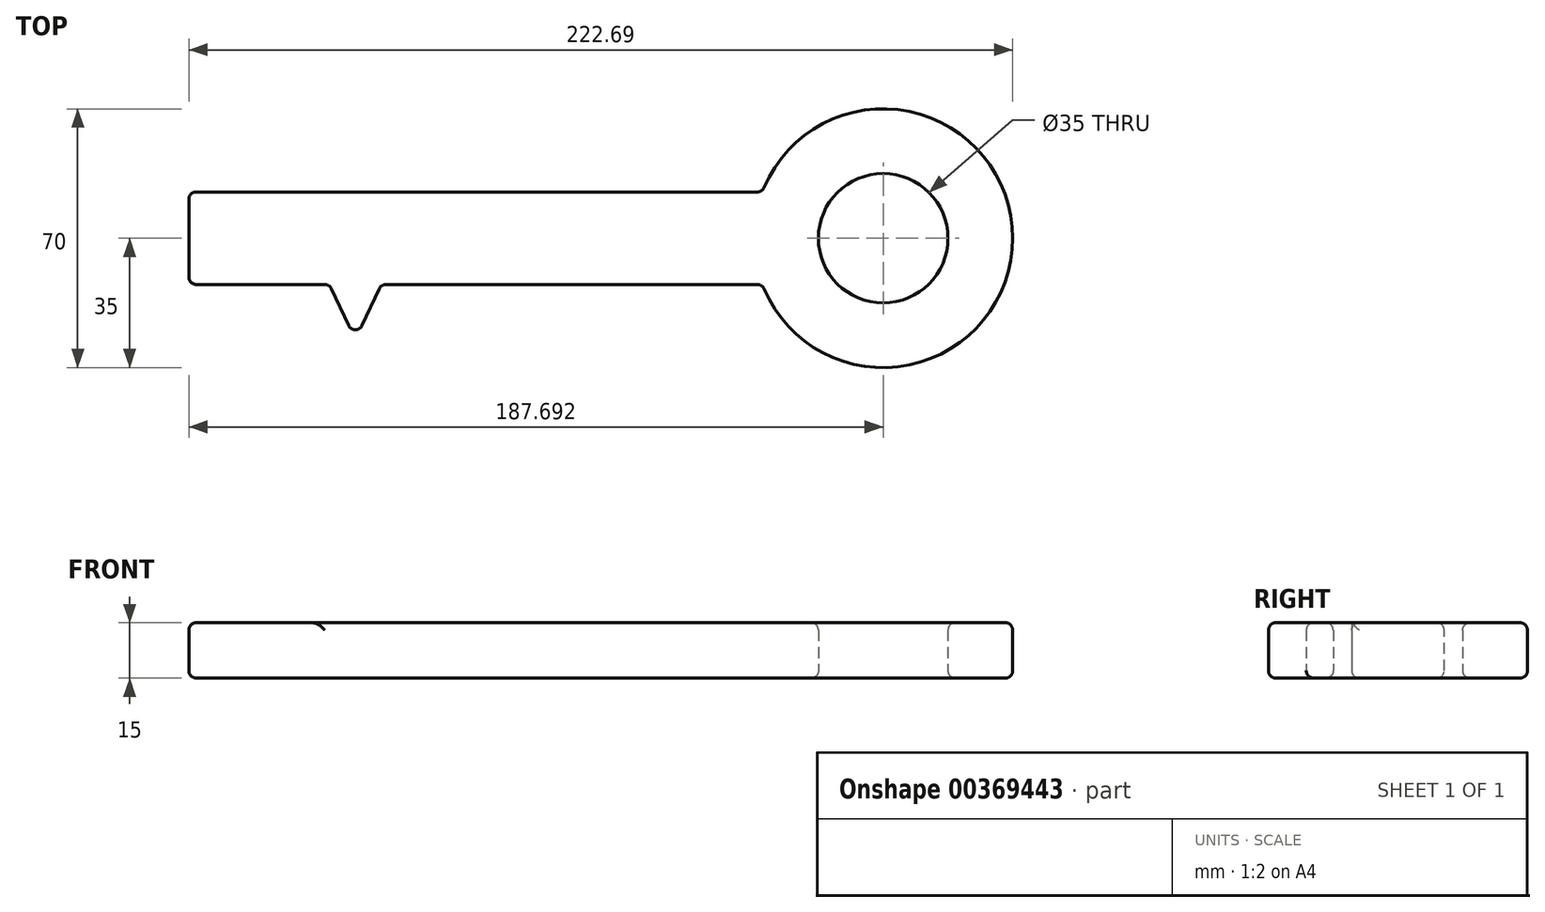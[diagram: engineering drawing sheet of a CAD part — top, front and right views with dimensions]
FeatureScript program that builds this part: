
annotation { "Feature Type Name" : "Feature", "Feature Type Description" : "" }
export const myFeature = defineFeature(function(context is Context, id is Id, definition is map)
    precondition{}
    {
        {
            var Q0;
            Q0=qCreatedBy(makeId("Top.planeOp"),FACE);
            var sketch = newSketch(context, id + "F0", { "sketchPlane" : qUnion([Q0])});
            skLineSegment(sketch, "E0.bottom", {"start": v(0, 10.7) * mm, "end": v(-155, 10.7) * mm});
            skLineSegment(sketch, "E0.top", {"start": v(0, 35.7) * mm, "end": v(-155, 35.7) * mm});
            skLineSegment(sketch, "E0.left", {"start": v(0, 10.7) * mm, "end": v(0, 35.7) * mm});
            skLineSegment(sketch, "E0.right", {"start": v(-155, 10.7) * mm, "end": v(-155, 35.7) * mm});
            skLineSegment(sketch, "E1.bottom", {"start": v(-155, 10.7) * mm, "end": v(-145, 10.7) * mm});
            skLineSegment(sketch, "E1.top", {"start": v(-155, -19.3) * mm, "end": v(-145, -19.3) * mm});
            skLineSegment(sketch, "E1.left", {"start": v(-155, 10.7) * mm, "end": v(-155, -19.3) * mm});
            skLineSegment(sketch, "E1.right", {"start": v(-145, 10.7) * mm, "end": v(-145, -19.3) * mm});
            skLineSegment(sketch, "E2.bottom", {"start": v(-135, 10.7) * mm, "end": v(-127, 10.7) * mm});
            skLineSegment(sketch, "E2.top", {"start": v(-135, -4.3) * mm, "end": v(-127, -4.3) * mm});
            skLineSegment(sketch, "E2.left", {"start": v(-135, 10.7) * mm, "end": v(-135, -4.3) * mm});
            skLineSegment(sketch, "E2.right", {"start": v(-127, 10.7) * mm, "end": v(-127, -4.3) * mm});
            skLineSegment(sketch, "E3", {"start": v(-103, 10.7) * mm, "end": v(-110, -4.3) * mm});
            skLineSegment(sketch, "E4", {"start": v(-110, -4.3) * mm, "end": v(-117, 10.7) * mm});
            skLineSegment(sketch, "E5", {"start": v(-117, 10.7) * mm, "end": v(-103, 10.7) * mm});
            skArc(sketch, "E6", {"start": v(0, 10.7) * mm, "mid": v(67.7, 23.2) * mm, "end": v(0, 35.7) * mm});
            skCircle(sketch, "E7", {"center": v(32.7, 23.2) * mm, "radius": 17.5 * mm});
            skLineSegment(sketch, "E8", {"start": v(32.7, 23.2) * mm, "end": v(-155, 23.2) * mm, "construction": true});
            skSolve(sketch);
        }
        {
            var Q0;
            Q0=makeQuery(id+"F0.imprint","IMPRINT",FACE,{"disambiguationData":[TD([[makeQuery(id+"F0.imprint","IMPRINT",EDGE,{"derivedFrom":sQuery(id+"F0.wireOp",EDGE,"E1.bottom")}),-1.0]])]});
            var Q1;
            Q1=makeQuery(id+"F0.imprint","IMPRINT",FACE,{"disambiguationData":[TD([[makeQuery(id+"F0.imprint","IMPRINT",EDGE,{"derivedFrom":sQuery(id+"F0.wireOp",EDGE,"E2.bottom")}),-1.0]])]});
            var Q2;
            Q2=makeQuery(id+"F0.imprint","IMPRINT",FACE,{"disambiguationData":[TD([[makeQuery(id+"F0.imprint","IMPRINT",EDGE,{"derivedFrom":sQuery(id+"F0.wireOp",EDGE,"E3")}),-1.0]])]});
            var Q3;
            Q3=makeQuery(id+"F0.imprint","IMPRINT",FACE,{"disambiguationData":[TD([[makeQuery(id+"F0.imprint","IMPRINT",EDGE,{"derivedFrom":sQuery(id+"F0.wireOp",EDGE,"E0.left")}),-1.0]])]});
            var Q4;
            Q4=makeQuery(id+"F0.imprint","IMPRINT",FACE,{"disambiguationData":[TD([[makeQuery(id+"F0.imprint","IMPRINT",EDGE,{"derivedFrom":sQuery(id+"F0.wireOp",EDGE,"E0.top")}),1.0]])]});
            extrude(context, id + "F1", {"entities" : qUnion([Q0, Q1, Q2, Q3, Q4]), "depth" : 15 * mm});
        }
        {
            var Q0;
            Q0=makeQuery(id+"F1.opExtrude","CAP_EDGE",EDGE,{"disambiguationData":[OSD([sQuery(id+"F0.wireOp",EDGE,"E0.top")])],"isStart":false});
            var Q1;
            Q1=makeQuery(id+"F1.opExtrude","CAP_EDGE",EDGE,{"disambiguationData":[OSD([sQuery(id+"F0.wireOp",EDGE,"E6")])],"isStart":false});
            var Q2;
            Q2=makeQuery(id+"F1.opExtrude","CAP_EDGE",EDGE,{"disambiguationData":[OSD([sQuery(id+"F0.wireOp",EDGE,"E7")])],"isStart":false});
            var Q3;
            {var subQ0=sQuery(id+"F0.wireOp",EDGE,"E0.bottom");Q3=makeQuery(id+"F1.opExtrude","CAP_EDGE",EDGE,{"disambiguationData":[OSD([subQ0]),TDD([makeQuery(id+"F0.imprint","IMPRINT",EDGE,{"disambiguationData":[TD([[makeQuery(id+"F0.imprint","INTERSECT",VERTEX,{"derivedFrom":[subQ0,sQuery(id+"F0.wireOp",EDGE,"E0.left"),sQuery(id+"F0.wireOp",EDGE,"E6")]}),-1.0]])],"derivedFrom":subQ0})])],"isStart":false});}
            var Q4;
            Q4=makeQuery(id+"F1.opExtrude","CAP_EDGE",EDGE,{"disambiguationData":[OSD([sQuery(id+"F0.wireOp",EDGE,"E3")])],"isStart":false});
            var Q5;
            Q5=makeQuery(id+"F1.opExtrude","CAP_EDGE",EDGE,{"disambiguationData":[OSD([sQuery(id+"F0.wireOp",EDGE,"E4")])],"isStart":false});
            var Q6;
            Q6=makeQuery(id+"F1.opExtrude","CAP_EDGE",EDGE,{"disambiguationData":[OSD([sQuery(id+"F0.wireOp",EDGE,"E2.right")])],"isStart":false});
            var Q7;
            Q7=makeQuery(id+"F1.opExtrude","CAP_EDGE",EDGE,{"disambiguationData":[OSD([sQuery(id+"F0.wireOp",EDGE,"E2.top")])],"isStart":false});
            var Q8;
            Q8=makeQuery(id+"F1.opExtrude","CAP_EDGE",EDGE,{"disambiguationData":[OSD([sQuery(id+"F0.wireOp",EDGE,"E2.left")])],"isStart":false});
            var Q9;
            Q9=makeQuery(id+"F1.opExtrude","CAP_EDGE",EDGE,{"disambiguationData":[OSD([sQuery(id+"F0.wireOp",EDGE,"E1.right")])],"isStart":false});
            var Q10;
            Q10=makeQuery(id+"F1.opExtrude","CAP_EDGE",EDGE,{"disambiguationData":[OSD([sQuery(id+"F0.wireOp",EDGE,"E1.top")])],"isStart":false});
            var Q11;
            Q11=makeQuery(id+"F1.opExtrude","CAP_EDGE",EDGE,{"disambiguationData":[OSD([sQuery(id+"F0.wireOp",EDGE,"E0.right"),sQuery(id+"F0.wireOp",EDGE,"E1.left")])],"isStart":false});
            var Q12;
            Q12=makeQuery(id+"F1.opExtrude","CAP_EDGE",EDGE,{"disambiguationData":[OSD([sQuery(id+"F0.wireOp",EDGE,"E0.top")])],"isStart":true});
            var Q13;
            Q13=makeQuery(id+"F1.opExtrude","CAP_EDGE",EDGE,{"disambiguationData":[OSD([sQuery(id+"F0.wireOp",EDGE,"E6")])],"isStart":true});
            var Q14;
            Q14=makeQuery(id+"F1.opExtrude","CAP_EDGE",EDGE,{"disambiguationData":[OSD([sQuery(id+"F0.wireOp",EDGE,"E7")])],"isStart":true});
            var Q15;
            Q15=makeQuery(id+"F1.opExtrude","SWEPT_EDGE",EDGE,{"disambiguationData":[OSD([sQuery(id+"F0.wireOp",EDGE,"E0.bottom"),sQuery(id+"F0.wireOp",EDGE,"E3"),sQuery(id+"F0.wireOp",EDGE,"E5")])]});
            var Q16;
            Q16=makeQuery(id+"F1.opExtrude","SWEPT_EDGE",EDGE,{"disambiguationData":[OSD([sQuery(id+"F0.wireOp",EDGE,"E3"),sQuery(id+"F0.wireOp",EDGE,"E4")])]});
            var Q17;
            Q17=makeQuery(id+"F1.opExtrude","SWEPT_EDGE",EDGE,{"disambiguationData":[OSD([sQuery(id+"F0.wireOp",EDGE,"E0.bottom"),sQuery(id+"F0.wireOp",EDGE,"E4"),sQuery(id+"F0.wireOp",EDGE,"E5")])]});
            var Q18;
            Q18=makeQuery(id+"F1.opExtrude","SWEPT_EDGE",EDGE,{"disambiguationData":[OSD([sQuery(id+"F0.wireOp",EDGE,"E2.top"),sQuery(id+"F0.wireOp",EDGE,"E2.right")])]});
            var Q19;
            Q19=makeQuery(id+"F1.opExtrude","SWEPT_EDGE",EDGE,{"disambiguationData":[OSD([sQuery(id+"F0.wireOp",EDGE,"E1.top"),sQuery(id+"F0.wireOp",EDGE,"E1.right")])]});
            var Q20;
            Q20=makeQuery(id+"F1.opExtrude","SWEPT_EDGE",EDGE,{"disambiguationData":[OSD([sQuery(id+"F0.wireOp",EDGE,"E2.top"),sQuery(id+"F0.wireOp",EDGE,"E2.left")])]});
            var Q21;
            Q21=makeQuery(id+"F1.opExtrude","SWEPT_EDGE",EDGE,{"disambiguationData":[OSD([sQuery(id+"F0.wireOp",EDGE,"E1.top"),sQuery(id+"F0.wireOp",EDGE,"E1.left")])]});
            var Q22;
            Q22=makeQuery(id+"F1.opExtrude","SWEPT_EDGE",EDGE,{"disambiguationData":[OSD([sQuery(id+"F0.wireOp",EDGE,"E0.bottom"),sQuery(id+"F0.wireOp",EDGE,"E0.left"),sQuery(id+"F0.wireOp",EDGE,"E6")])]});
            var Q23;
            {var subQ0=sQuery(id+"F0.wireOp",EDGE,"E0.bottom");Q23=makeQuery(id+"F1.opExtrude","SWEPT_FACE",FACE,{"disambiguationData":[OSD([subQ0]),TDD([makeQuery(id+"F0.imprint","IMPRINT",EDGE,{"disambiguationData":[TD([[makeQuery(id+"F0.imprint","INTERSECT",VERTEX,{"derivedFrom":[subQ0,sQuery(id+"F0.wireOp",EDGE,"E0.left"),sQuery(id+"F0.wireOp",EDGE,"E6")]}),-1.0]])],"derivedFrom":subQ0})])]});}
            var Q24;
            {var subQ0=sQuery(id+"F0.wireOp",EDGE,"E0.bottom");Q24=makeQuery(id+"F1.opExtrude","CAP_EDGE",EDGE,{"disambiguationData":[OSD([subQ0]),TDD([makeQuery(id+"F0.imprint","IMPRINT",EDGE,{"disambiguationData":[TD([[makeQuery(id+"F0.imprint","INTERSECT",VERTEX,{"derivedFrom":[subQ0,sQuery(id+"F0.wireOp",EDGE,"E0.left"),sQuery(id+"F0.wireOp",EDGE,"E6")]}),-1.0]])],"derivedFrom":subQ0})])],"isStart":true});}
            var Q25;
            Q25=makeQuery(id+"F1.opExtrude","CAP_EDGE",EDGE,{"disambiguationData":[OSD([sQuery(id+"F0.wireOp",EDGE,"E3")])],"isStart":true});
            var Q26;
            Q26=makeQuery(id+"F1.opExtrude","CAP_EDGE",EDGE,{"disambiguationData":[OSD([sQuery(id+"F0.wireOp",EDGE,"E4")])],"isStart":true});
            var Q27;
            Q27=makeQuery(id+"F1.opExtrude","CAP_EDGE",EDGE,{"disambiguationData":[OSD([sQuery(id+"F0.wireOp",EDGE,"E2.top")])],"isStart":true});
            var Q28;
            Q28=makeQuery(id+"F1.opExtrude","CAP_EDGE",EDGE,{"disambiguationData":[OSD([sQuery(id+"F0.wireOp",EDGE,"E1.top")])],"isStart":true});
            var Q29;
            {var subQ0=sQuery(id+"F0.wireOp",EDGE,"E0.bottom");Q29=makeQuery(id+"F1.opExtrude","CAP_EDGE",EDGE,{"disambiguationData":[OSD([subQ0]),TDD([makeQuery(id+"F0.imprint","IMPRINT",EDGE,{"disambiguationData":[TD([[makeQuery(id+"F0.imprint","INTERSECT",VERTEX,{"derivedFrom":[subQ0,sQuery(id+"F0.wireOp",EDGE,"E2.bottom"),sQuery(id+"F0.wireOp",EDGE,"E2.right")]}),1.0]])],"derivedFrom":subQ0})])],"isStart":true});}
            var Q30;
            {var subQ0=sQuery(id+"F0.wireOp",EDGE,"E0.bottom");Q30=makeQuery(id+"F1.opExtrude","CAP_EDGE",EDGE,{"disambiguationData":[OSD([subQ0]),TDD([makeQuery(id+"F0.imprint","IMPRINT",EDGE,{"disambiguationData":[TD([[makeQuery(id+"F0.imprint","INTERSECT",VERTEX,{"derivedFrom":[subQ0,sQuery(id+"F0.wireOp",EDGE,"E1.bottom"),sQuery(id+"F0.wireOp",EDGE,"E1.right")]}),1.0]])],"derivedFrom":subQ0})])],"isStart":true});}
            var Q31;
            Q31=makeQuery(id+"F1.opExtrude","CAP_EDGE",EDGE,{"disambiguationData":[OSD([sQuery(id+"F0.wireOp",EDGE,"E0.right"),sQuery(id+"F0.wireOp",EDGE,"E1.left")])],"isStart":true});
            var Q32;
            Q32=makeQuery(id+"F1.opExtrude","SWEPT_EDGE",EDGE,{"disambiguationData":[OSD([sQuery(id+"F0.wireOp",EDGE,"E0.top"),sQuery(id+"F0.wireOp",EDGE,"E0.right")])]});
            var Q33;
            Q33=makeQuery(id+"F1.opExtrude","SWEPT_FACE",FACE,{"disambiguationData":[OSD([sQuery(id+"F0.wireOp",EDGE,"E6")])]});
            fillet(context, id + "F2", {"entities" : qUnion([Q0, Q1, Q2, Q3, Q4, Q5, Q6, Q7, Q8, Q9, Q10, Q11, Q12, Q13, Q14, Q15, Q16, Q17, Q18, Q19, Q20, Q21, Q22, Q23, Q24, Q25, Q26, Q27, Q28, Q29, Q30, Q31, Q32, Q33]), "radius" : 2 * mm, "tangentPropagation" : true, "allowEdgeOverflow" : false});
        }
    });
